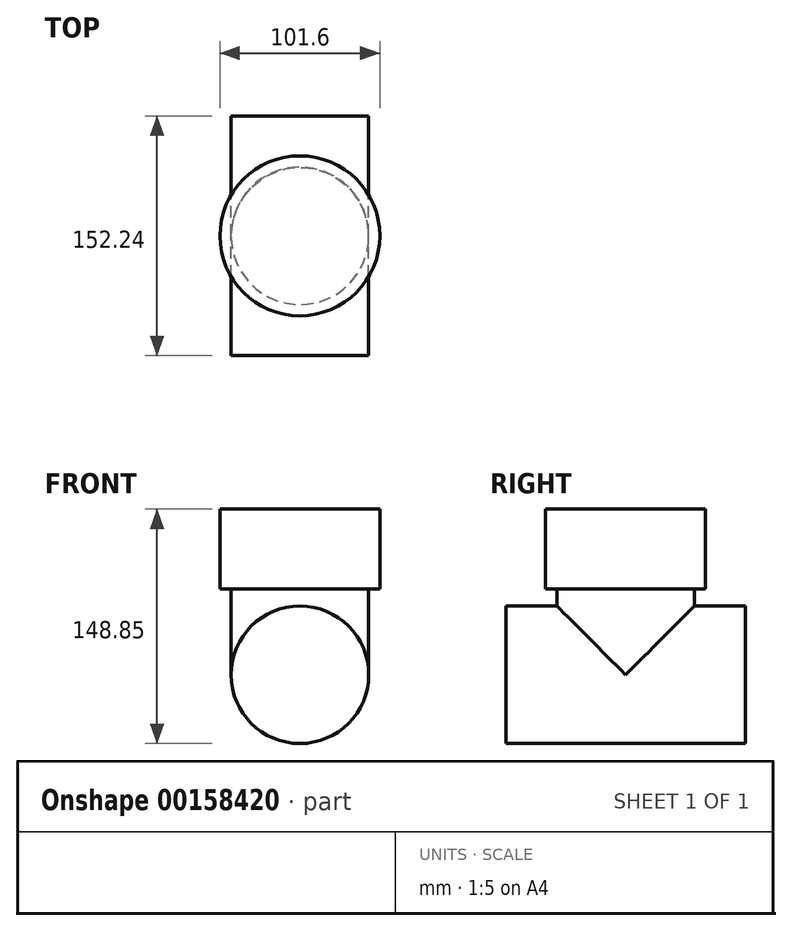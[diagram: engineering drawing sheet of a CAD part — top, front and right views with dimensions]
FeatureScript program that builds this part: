
annotation { "Feature Type Name" : "Feature", "Feature Type Description" : "" }
export const myFeature = defineFeature(function(context is Context, id is Id, definition is map)
    precondition{}
    {
        {
            var Q0;
            Q0=qCreatedBy(makeId("Front.planeOp"),FACE);
            var sketch = newSketch(context, id + "F0", { "sketchPlane" : qUnion([Q0])});
            skCircle(sketch, "E0", {"center": v(0, 0) * mm, "radius": 43.69 * mm});
            skSolve(sketch);
        }
        {
            var Q0;
            Q0=qCreatedBy(makeId("Top.planeOp"),FACE);
            var sketch = newSketch(context, id + "F1", { "sketchPlane" : qUnion([Q0])});
            skCircle(sketch, "E1", {"center": v(0, 0) * mm, "radius": 43.69 * mm});
            skSolve(sketch);
        }
        {
            var Q0;
            Q0=makeQuery(id+"F0.imprint","IMPRINT",FACE,{"disambiguationData":[TD([[makeQuery(id+"F0.imprint","IMPRINT",EDGE,{"derivedFrom":sQuery(id+"F0.wireOp",EDGE,"E0")}),1.0]])]});
            extrude(context, id + "F2", {"entities" : qUnion([Q0]), "depth" : 76.12 * mm, "hasSecondDirection" : true, "secondDirectionOppositeDirection" : true, "secondDirectionDepth" : 76.12 * mm});
        }
        {
            var Q0;
            Q0 = qSketchRegion(id + "F1", true);
            extrude(context, id + "F3", {"entities" : qUnion([Q0]), "operationType" : NewBodyOperationType.ADD, "depth" : 54.36 * mm});
        }
        {
            var Q0;
            Q0=makeQuery(id+"F3.opExtrude","CAP_FACE",FACE,{"disambiguationData":[OSD([sQuery(id+"F1.wireOp",EDGE,"E1")])],"isStart":false});
            var sketch = newSketch(context, id + "F4", { "sketchPlane" : qUnion([Q0])});
            skCircle(sketch, "E2", {"center": v(0, 0) * mm, "radius": 50.8 * mm});
            skSolve(sketch);
        }
        {
            var Q0;
            Q0=makeQuery(id+"F4.imprint","IMPRINT",FACE,{"disambiguationData":[TD([[makeQuery(id+"F4.imprint","IMPRINT",EDGE,{"derivedFrom":makeQuery(id+"F3.opExtrude","CAP_EDGE",EDGE,{"disambiguationData":[OSD([sQuery(id+"F1.wireOp",EDGE,"E1")])],"isStart":false})}),1.0]])]});
            var Q1;
            Q1=makeQuery(id+"F4.imprint","IMPRINT",FACE,{"disambiguationData":[TD([[makeQuery(id+"F4.imprint","IMPRINT",EDGE,{"derivedFrom":sQuery(id+"F4.wireOp",EDGE,"E2")}),1.0]])]});
            extrude(context, id + "F5", {"entities" : qUnion([Q0, Q1]), "operationType" : NewBodyOperationType.ADD, "depth" : 50.8 * mm});
        }
    });
